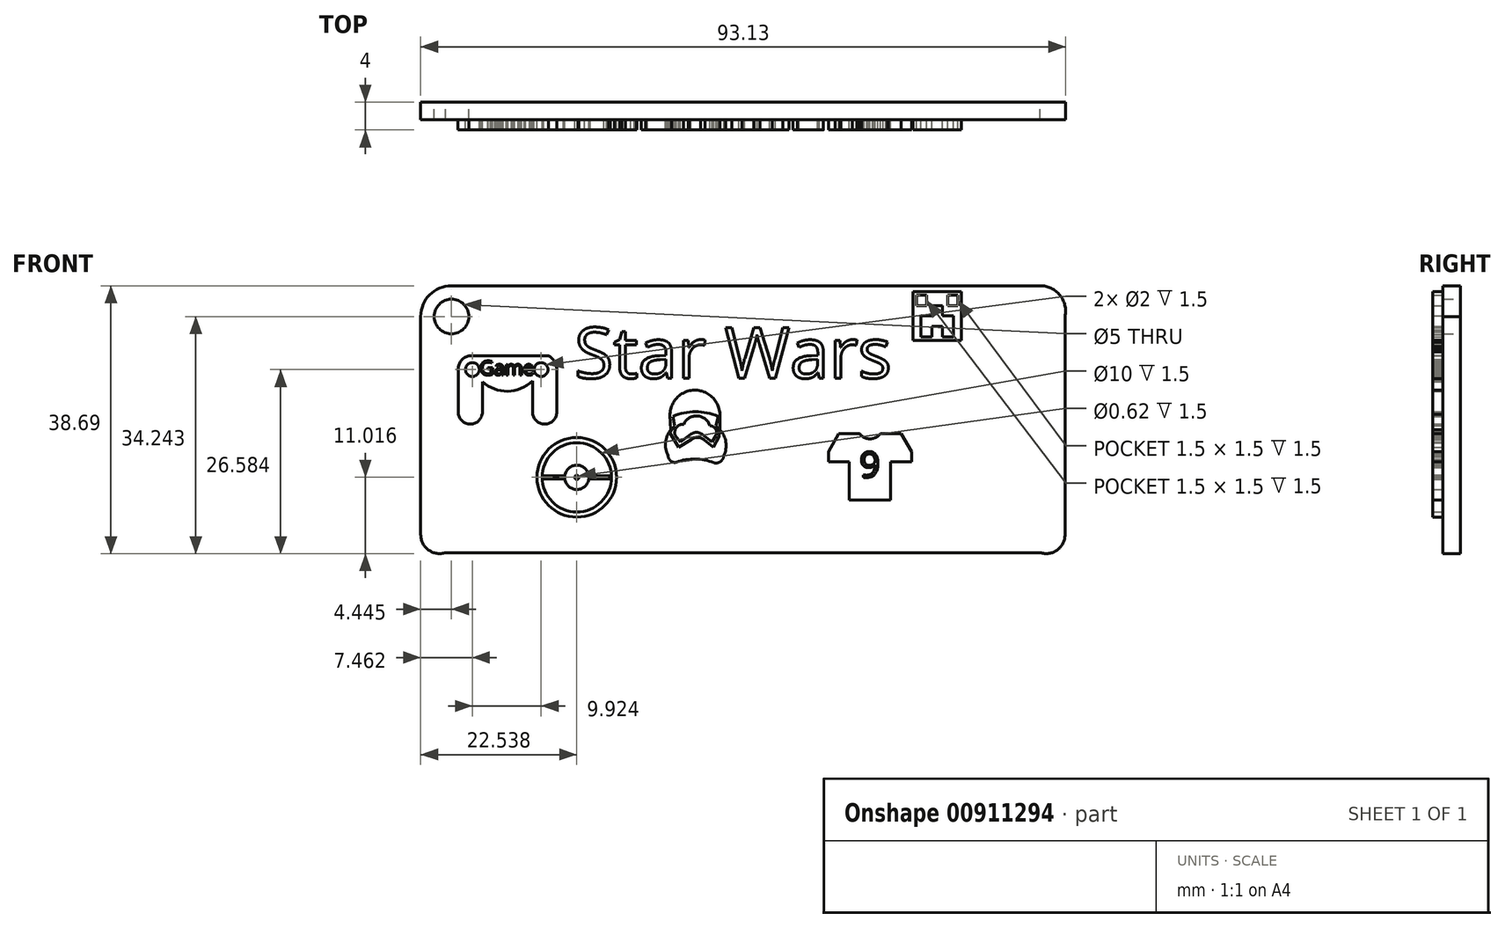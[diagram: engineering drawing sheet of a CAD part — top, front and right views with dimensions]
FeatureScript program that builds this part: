
annotation { "Feature Type Name" : "Feature", "Feature Type Description" : "" }
export const myFeature = defineFeature(function(context is Context, id is Id, definition is map)
    precondition{}
    {
        {
            var Q0;
            Q0=qCreatedBy(makeId("Front.planeOp"),FACE);
            var sketch = newSketch(context, id + "F0", { "sketchPlane" : qUnion([Q0])});
            skLineSegment(sketch, "E0", {"start": v(-44.85, 33.29) * mm, "end": v(40.15, 33.29) * mm});
            skLineSegment(sketch, "E1", {"start": v(-49.3, 28.84) * mm, "end": v(-49.3, -2.66) * mm});
            skLineSegment(sketch, "E2", {"start": v(-45.7, -5.26) * mm, "end": v(40.15, -5.26) * mm});
            skLineSegment(sketch, "E3", {"start": v(43.75, -2.66) * mm, "end": v(43.75, 28.84) * mm});
            skArc(sketch, "E4", {"start": v(-44.85, 33.29) * mm, "mid": v(-48, 31.99) * mm, "end": v(-49.3, 28.84) * mm});
            skArc(sketch, "E5", {"start": v(43.75, 28.84) * mm, "mid": v(43, 31.92) * mm, "end": v(40.15, 33.29) * mm});
            skArc(sketch, "E6", {"start": v(-49.3, -2.66) * mm, "mid": v(-48.16, -4.88) * mm, "end": v(-45.7, -5.26) * mm});
            skArc(sketch, "E7", {"start": v(40.15, -5.26) * mm, "mid": v(42.61, -4.88) * mm, "end": v(43.75, -2.66) * mm});
            skCircle(sketch, "E8", {"center": v(-44.85, 28.84) * mm, "radius": 2.5 * mm});
            skSolve(sketch);
        }
        {
            var Q0;
            Q0 = qSketchRegion(id + "F0", true);
            extrude(context, id + "F1", {"entities" : qUnion([Q0]), "depth" : 2.5 * mm, "offsetDistance" : 25 * mm});
        }
        {
            var Q0;
            Q0=makeQuery(id+"F1.opExtrude","CAP_FACE",FACE,{"disambiguationData":[OSD([sQuery(id+"F0.wireOp",EDGE,"E0"),sQuery(id+"F0.wireOp",EDGE,"E1"),sQuery(id+"F0.wireOp",EDGE,"E2"),sQuery(id+"F0.wireOp",EDGE,"E3"),sQuery(id+"F0.wireOp",EDGE,"E4"),sQuery(id+"F0.wireOp",EDGE,"E5"),sQuery(id+"F0.wireOp",EDGE,"E6"),sQuery(id+"F0.wireOp",EDGE,"E7"),sQuery(id+"F0.wireOp",EDGE,"E8")])],"isStart":false});
            var sketch = newSketch(context, id + "F2", { "sketchPlane" : qUnion([Q0])});
            skLineSegment(sketch, "E9", {"start": v(-42.35, 23.18) * mm, "end": v(-30.85, 23.18) * mm});
            skArc(sketch, "E10", {"start": v(-42.35, 23.18) * mm, "mid": v(-43.5, 22.4) * mm, "end": v(-43.9, 21.05) * mm});
            skArc(sketch, "E11", {"start": v(-30.85, 23.18) * mm, "mid": v(-29.94, 22.3) * mm, "end": v(-29.65, 21.05) * mm});
            skLineSegment(sketch, "E12", {"start": v(-43.9, 21.05) * mm, "end": v(-43.9, 15.05) * mm});
            skLineSegment(sketch, "E13", {"start": v(-29.65, 21.05) * mm, "end": v(-29.65, 15.05) * mm});
            skLineSegment(sketch, "E14", {"start": v(-40.4, 19.42) * mm, "end": v(-40.4, 15.05) * mm});
            skLineSegment(sketch, "E15", {"start": v(-33.15, 19.55) * mm, "end": v(-33.15, 15.05) * mm});
            skArc(sketch, "E16", {"start": v(-43.9, 15.05) * mm, "mid": v(-42.15, 13.3) * mm, "end": v(-40.4, 15.05) * mm});
            skArc(sketch, "E17", {"start": v(-33.15, 15.05) * mm, "mid": v(-31.4, 13.3) * mm, "end": v(-29.65, 15.05) * mm});
            skCircle(sketch, "E18", {"center": v(-31.91, 21.18) * mm, "radius": 1 * mm});
            skCircle(sketch, "E19", {"center": v(-41.84, 21.18) * mm, "radius": 1 * mm});
            skArc(sketch, "E20", {"start": v(-40.4, 19.42) * mm, "mid": v(-36.75, 18.05) * mm, "end": v(-33.15, 19.55) * mm});
            skText(sketch, "E21", { "text": "Game\n", "fontName": "OpenSans-Regular.ttf"});
            skLineSegment(sketch, "E22.bottom", {"start": v(21.78, 32.42) * mm, "end": v(28.78, 32.42) * mm});
            skLineSegment(sketch, "E22.top", {"start": v(21.78, 25.42) * mm, "end": v(28.78, 25.42) * mm});
            skLineSegment(sketch, "E22.left", {"start": v(21.78, 32.42) * mm, "end": v(21.78, 25.42) * mm});
            skLineSegment(sketch, "E22.right", {"start": v(28.78, 32.42) * mm, "end": v(28.78, 25.42) * mm});
            skLineSegment(sketch, "E23.bottom", {"start": v(22.28, 31.92) * mm, "end": v(23.78, 31.92) * mm});
            skLineSegment(sketch, "E23.top", {"start": v(22.28, 30.42) * mm, "end": v(23.78, 30.42) * mm});
            skLineSegment(sketch, "E23.left", {"start": v(22.28, 31.92) * mm, "end": v(22.28, 30.42) * mm});
            skLineSegment(sketch, "E23.right", {"start": v(23.78, 31.92) * mm, "end": v(23.78, 30.42) * mm});
            skLineSegment(sketch, "E24.bottom", {"start": v(26.78, 31.92) * mm, "end": v(28.28, 31.92) * mm});
            skLineSegment(sketch, "E24.top", {"start": v(26.78, 30.42) * mm, "end": v(28.28, 30.42) * mm});
            skLineSegment(sketch, "E24.left", {"start": v(26.78, 31.92) * mm, "end": v(26.78, 30.42) * mm});
            skLineSegment(sketch, "E24.right", {"start": v(28.28, 31.92) * mm, "end": v(28.28, 30.42) * mm});
            skLineSegment(sketch, "E25.bottom", {"start": v(24.53, 30.42) * mm, "end": v(26.03, 30.42) * mm});
            skLineSegment(sketch, "E25.left", {"start": v(24.53, 30.42) * mm, "end": v(24.53, 28.92) * mm});
            skLineSegment(sketch, "E25.right", {"start": v(26.03, 30.42) * mm, "end": v(26.03, 28.92) * mm});
            skLineSegment(sketch, "E26", {"start": v(24.53, 28.92) * mm, "end": v(22.93, 28.92) * mm});
            skLineSegment(sketch, "E27", {"start": v(22.93, 25.92) * mm, "end": v(22.93, 28.92) * mm});
            skLineSegment(sketch, "E28", {"start": v(27.63, 25.92) * mm, "end": v(27.63, 28.92) * mm});
            skLineSegment(sketch, "E29", {"start": v(27.63, 28.92) * mm, "end": v(26.03, 28.92) * mm});
            skLineSegment(sketch, "E30", {"start": v(24.53, 25.92) * mm, "end": v(22.93, 25.92) * mm});
            skLineSegment(sketch, "E31", {"start": v(27.63, 25.92) * mm, "end": v(26.03, 25.92) * mm});
            skPoint(sketch, "E32", {"position": v(22.93, 27.42) * mm});
            skLineSegment(sketch, "E33", {"start": v(24.53, 25.92) * mm, "end": v(24.53, 27.42) * mm});
            skLineSegment(sketch, "E34", {"start": v(26.03, 27.42) * mm, "end": v(24.53, 27.42) * mm});
            skLineSegment(sketch, "E35", {"start": v(26.03, 27.42) * mm, "end": v(26.03, 25.92) * mm});
            const initialGuessF2  = {"E21": [-0.0408, 0.0204, 1, 0, 0.00204]};
            skSetInitialGuess(sketch, initialGuessF2);
            skSolve(sketch);
        }
        {
            var Q0;
            Q0=makeQuery(id+"F2.imprint","IMPRINT",FACE,{"disambiguationData":[TD([[makeQuery(id+"F2.imprint","IMPRINT",EDGE,{"derivedFrom":sQuery(id+"F2.wireOp",EDGE,"E21.sketch_text.stroke-89")}),1.0]])]});
            var Q1;
            Q1=makeQuery(id+"F2.imprint","IMPRINT",FACE,{"disambiguationData":[TD([[makeQuery(id+"F2.imprint","IMPRINT",EDGE,{"derivedFrom":sQuery(id+"F2.wireOp",EDGE,"E21.sketch_text.stroke-39")}),1.0]])]});
            var Q2;
            Q2=makeQuery(id+"F2.imprint","IMPRINT",FACE,{"disambiguationData":[TD([[makeQuery(id+"F2.imprint","IMPRINT",EDGE,{"derivedFrom":sQuery(id+"F2.wireOp",EDGE,"E9")}),-1.0]])]});
            var Q3;
            Q3=makeQuery(id+"F2.imprint","IMPRINT",FACE,{"disambiguationData":[TD([[makeQuery(id+"F2.imprint","IMPRINT",EDGE,{"derivedFrom":sQuery(id+"F2.wireOp",EDGE,"E22.bottom")}),-1.0]])]});
            extrude(context, id + "F3", {"entities" : qUnion([Q0, Q1, Q2, Q3]), "operationType" : NewBodyOperationType.ADD, "depth" : 1.5 * mm, "offsetDistance" : 25 * mm});
        }
        {
            var Q0;
            {var subQ0=sQuery(id+"F0.wireOp",EDGE,"E1");var subQ1=sQuery(id+"F0.wireOp",EDGE,"E3");var subQ2=sQuery(id+"F0.wireOp",EDGE,"E0");var subQ3=sQuery(id+"F0.wireOp",EDGE,"E4");var subQ4=sQuery(id+"F0.wireOp",EDGE,"E5");var subQ5=sQuery(id+"F0.wireOp",EDGE,"E6");var subQ6=sQuery(id+"F0.wireOp",EDGE,"E7");var subQ7=sQuery(id+"F0.wireOp",EDGE,"E8");var subQ8=sQuery(id+"F0.wireOp",EDGE,"E2");Q0=makeQuery(id+"F3.boolean.opBoolean","SPLIT",FACE,{"disambiguationData":[TD([makeQuery(id+"F1.opExtrude","SWEPT_FACE",FACE,{"disambiguationData":[OSD([subQ2])]})])],"derivedFrom":makeQuery(id+"F1.opExtrude","CAP_FACE",FACE,{"disambiguationData":[OSD([subQ2,subQ0,subQ8,subQ1,subQ3,subQ4,subQ5,subQ6,subQ7])],"isStart":false})});}
            var sketch = newSketch(context, id + "F4", { "sketchPlane" : qUnion([Q0])});
            skLineSegment(sketch, "E36", {"start": v(11.07, 11.93) * mm, "end": v(14.07, 11.93) * mm});
            skLineSegment(sketch, "E37", {"start": v(17.07, 11.93) * mm, "end": v(20.07, 11.93) * mm});
            skLineSegment(sketch, "E38", {"start": v(20.07, 11.93) * mm, "end": v(21.57, 9.33) * mm});
            skLineSegment(sketch, "E39", {"start": v(21.57, 9.33) * mm, "end": v(21.57, 7.83) * mm});
            skPoint(sketch, "E40", {"position": v(18.57, 11.93) * mm});
            skPoint(sketch, "E41", {"position": v(12.57, 11.93) * mm});
            skLineSegment(sketch, "E42", {"start": v(21.57, 7.83) * mm, "end": v(18.57, 7.83) * mm});
            skLineSegment(sketch, "E43", {"start": v(18.57, 7.83) * mm, "end": v(18.57, 2.33) * mm});
            skLineSegment(sketch, "E44", {"start": v(18.57, 2.33) * mm, "end": v(12.57, 2.33) * mm});
            skLineSegment(sketch, "E45", {"start": v(12.57, 2.33) * mm, "end": v(12.57, 7.83) * mm});
            skLineSegment(sketch, "E46", {"start": v(12.57, 7.83) * mm, "end": v(9.57, 7.83) * mm});
            skLineSegment(sketch, "E47", {"start": v(9.57, 7.83) * mm, "end": v(9.57, 9.33) * mm});
            skLineSegment(sketch, "E48", {"start": v(9.57, 9.33) * mm, "end": v(11.07, 11.93) * mm});
            skArc(sketch, "E49", {"start": v(14.07, 11.93) * mm, "mid": v(15.57, 11.18) * mm, "end": v(17.07, 11.93) * mm});
            skText(sketch, "E50", { "text": "9\n", "fontName": "OpenSans-Regular.ttf"});
            skCircle(sketch, "E51", {"center": v(-26.76, 5.62) * mm, "radius": 5 * mm});
            skCircle(sketch, "E52", {"center": v(-26.76, 5.62) * mm, "radius": 1.75 * mm});
            skLineSegment(sketch, "E53.left", {"start": v(-25.03, 5.4) * mm, "end": v(-25.03, 5.85) * mm});
            skLineSegment(sketch, "E53.right", {"start": v(-21.77, 5.4) * mm, "end": v(-21.77, 5.85) * mm});
            skLineSegment(sketch, "E54.left", {"start": v(-28.5, 5.4) * mm, "end": v(-28.5, 5.85) * mm});
            skLineSegment(sketch, "E54.right", {"start": v(-31.76, 5.4) * mm, "end": v(-31.76, 5.85) * mm});
            skCircle(sketch, "E55", {"center": v(-26.76, 5.62) * mm, "radius": 5.75 * mm});
            skLineSegment(sketch, "E56.bottom", {"start": v(-21.96, 5.4) * mm, "end": v(-24.81, 5.4) * mm});
            skLineSegment(sketch, "E56.top", {"start": v(-21.96, 5.85) * mm, "end": v(-24.81, 5.85) * mm});
            skLineSegment(sketch, "E56.left", {"start": v(-21.96, 5.4) * mm, "end": v(-21.96, 5.85) * mm});
            skLineSegment(sketch, "E56.right", {"start": v(-24.81, 5.4) * mm, "end": v(-24.81, 5.85) * mm});
            skLineSegment(sketch, "E57.bottom", {"start": v(-28.71, 5.4) * mm, "end": v(-31.56, 5.4) * mm});
            skLineSegment(sketch, "E57.top", {"start": v(-28.71, 5.85) * mm, "end": v(-31.56, 5.85) * mm});
            skLineSegment(sketch, "E57.left", {"start": v(-28.71, 5.4) * mm, "end": v(-28.71, 5.85) * mm});
            skLineSegment(sketch, "E57.right", {"start": v(-31.56, 5.4) * mm, "end": v(-31.56, 5.85) * mm});
            skCircle(sketch, "E58", {"center": v(-26.76, 5.62) * mm, "radius": 0.3 * mm});
            const initialGuessF4  = {"E50": [0.01407, 0.00563, 1, 0, 0.0037]};
            skSetInitialGuess(sketch, initialGuessF4);
            skSolve(sketch);
        }
        {
            var Q0;
            Q0=makeQuery(id+"F4.imprint","IMPRINT",FACE,{"disambiguationData":[TD([[makeQuery(id+"F4.imprint","IMPRINT",EDGE,{"derivedFrom":sQuery(id+"F4.wireOp",EDGE,"E36")}),-1.0]])]});
            var Q1;
            Q1=makeQuery(id+"F4.imprint","IMPRINT",FACE,{"disambiguationData":[TD([[makeQuery(id+"F4.imprint","IMPRINT",EDGE,{"derivedFrom":sQuery(id+"F4.wireOp",EDGE,"E50.sketch_text.stroke-16")}),1.0]])]});
            var Q2;
            Q2=makeQuery(id+"F4.imprint","IMPRINT",FACE,{"disambiguationData":[TD([[makeQuery(id+"F4.imprint","IMPRINT",EDGE,{"derivedFrom":sQuery(id+"F4.wireOp",EDGE,"E55")}),1.0]])]});
            var Q3;
            {var subQ0=sQuery(id+"F4.wireOp",EDGE,"E54.left");var subQ1=sQuery(id+"F4.wireOp",EDGE,"E52");var subQ2=makeQuery(id+"F4.imprint","INTERSECT",VERTEX,{"derivedFrom":[subQ1,subQ0]});Q3=makeQuery(id+"F4.imprint","IMPRINT",FACE,{"disambiguationData":[TD([[makeQuery(id+"F4.imprint","IMPRINT",EDGE,{"disambiguationData":[TD([[subQ2,1.0]])],"derivedFrom":subQ1}),1.0]])]});}
            var Q4;
            {var subQ4=sQuery(id+"F4.wireOp",EDGE,"E54.bottom");Q4=makeQuery(id+"F4.imprint","IMPRINT",FACE,{"disambiguationData":[TD([[makeQuery(id+"F4.imprint","IMPRINT",EDGE,{"derivedFrom":subQ4}),-1.0]])]});}
            var Q5;
            {var subQ4=sQuery(id+"F4.wireOp",EDGE,"E53.bottom");Q5=makeQuery(id+"F4.imprint","IMPRINT",FACE,{"disambiguationData":[TD([[makeQuery(id+"F4.imprint","IMPRINT",EDGE,{"derivedFrom":subQ4}),1.0]])]});}
            var Q6;
            Q6=makeQuery(id+"F4.imprint","IMPRINT",FACE,{"disambiguationData":[TD([[makeQuery(id+"F4.imprint","IMPRINT",EDGE,{"derivedFrom":sQuery(id+"F4.wireOp",EDGE,"E57.bottom")}),-1.0]])]});
            var Q7;
            {var subQ0=sQuery(id+"F4.wireOp",EDGE,"E54.left");var subQ1=sQuery(id+"F4.wireOp",EDGE,"E52");var subQ2=makeQuery(id+"F4.imprint","INTERSECT",VERTEX,{"disambiguationData":[OD(1.0)],"derivedFrom":[subQ1,subQ0]});Q7=makeQuery(id+"F4.imprint","IMPRINT",FACE,{"disambiguationData":[TD([[makeQuery(id+"F4.imprint","IMPRINT",EDGE,{"disambiguationData":[TD([[subQ2,1.0]])],"derivedFrom":subQ1}),1.0]])]});}
            var Q8;
            Q8=makeQuery(id+"F4.imprint","IMPRINT",FACE,{"disambiguationData":[TD([[makeQuery(id+"F4.imprint","IMPRINT",EDGE,{"derivedFrom":sQuery(id+"F4.wireOp",EDGE,"E56.bottom")}),-1.0]])]});
            extrude(context, id + "F5", {"entities" : qUnion([Q0, Q1, Q2, Q3, Q4, Q5, Q6, Q7, Q8]), "operationType" : NewBodyOperationType.ADD, "depth" : 1.5 * mm, "offsetDistance" : 25 * mm});
        }
        {
            var Q0;
            {var subQ6=sQuery(id+"F0.wireOp",EDGE,"E1");var subQ9=sQuery(id+"F0.wireOp",EDGE,"E3");var subQ11=sQuery(id+"F0.wireOp",EDGE,"E0");var subQ12=makeQuery(id+"F1.opExtrude","SWEPT_FACE",FACE,{"disambiguationData":[OSD([subQ11])]});var subQ13=sQuery(id+"F0.wireOp",EDGE,"E4");var subQ16=sQuery(id+"F0.wireOp",EDGE,"E5");var subQ19=sQuery(id+"F0.wireOp",EDGE,"E6");var subQ22=sQuery(id+"F0.wireOp",EDGE,"E7");var subQ25=sQuery(id+"F0.wireOp",EDGE,"E8");var subQ28=sQuery(id+"F0.wireOp",EDGE,"E2");Q0=makeQuery(id+"F5.boolean.opBoolean","SPLIT",FACE,{"disambiguationData":[TD([subQ12])],"derivedFrom":makeQuery(id+"F3.boolean.opBoolean","SPLIT",FACE,{"disambiguationData":[TD([subQ12])],"derivedFrom":makeQuery(id+"F1.opExtrude","CAP_FACE",FACE,{"disambiguationData":[OSD([subQ11,subQ6,subQ28,subQ9,subQ13,subQ16,subQ19,subQ22,subQ25])],"isStart":false})})});}
            var sketch = newSketch(context, id + "F6", { "sketchPlane" : qUnion([Q0])});
            skText(sketch, "E59", { "text": "Star Wars\n", "fontName": "OpenSans-Regular.ttf"});
            skArc(sketch, "E60", {"start": v(-6.1, 14.7) * mm, "mid": v(-9.8, 18.21) * mm, "end": v(-13.3, 14.51) * mm});
            skArc(sketch, "E61", {"start": v(-6.96, 7.7) * mm, "mid": v(-9.67, 8.26) * mm, "end": v(-12.4, 7.79) * mm});
            skArc(sketch, "E62", {"start": v(-13.18, 12.52) * mm, "mid": v(-13.94, 10.68) * mm, "end": v(-13.56, 8.74) * mm});
            skLineSegment(sketch, "E63", {"start": v(-13.3, 14.51) * mm, "end": v(-13.18, 12.52) * mm});
            skArc(sketch, "E64", {"start": v(-13.56, 8.74) * mm, "mid": v(-13.2, 7.98) * mm, "end": v(-12.4, 7.79) * mm});
            skArc(sketch, "E65", {"start": v(-5.53, 8.73) * mm, "mid": v(-5.24, 10.7) * mm, "end": v(-6.1, 12.52) * mm});
            skArc(sketch, "E66", {"start": v(-6.96, 7.7) * mm, "mid": v(-6.01, 7.9) * mm, "end": v(-5.53, 8.73) * mm});
            skLineSegment(sketch, "E67", {"start": v(-12.65, 13.06) * mm, "end": v(-13.3, 12.03) * mm});
            skLineSegment(sketch, "E68", {"start": v(-13.3, 12.03) * mm, "end": v(-12.06, 9.97) * mm});
            skLineSegment(sketch, "E69", {"start": v(-6.1, 12.52) * mm, "end": v(-6.1, 14.7) * mm});
            skLineSegment(sketch, "E70", {"start": v(-6.22, 11.51) * mm, "end": v(-7.02, 9.97) * mm});
            skLineSegment(sketch, "E71", {"start": v(-12.06, 9.97) * mm, "end": v(-10.28, 11.04) * mm});
            skLineSegment(sketch, "E72", {"start": v(-7.02, 9.97) * mm, "end": v(-8.34, 11.04) * mm});
            skArc(sketch, "E73", {"start": v(-8.34, 11.04) * mm, "mid": v(-9.31, 11.38) * mm, "end": v(-10.28, 11.04) * mm});
            skArc(sketch, "E74", {"start": v(-7.53, 13.06) * mm, "mid": v(-9.35, 14.5) * mm, "end": v(-11.32, 13.28) * mm});
            skArc(sketch, "E75", {"start": v(-6.69, 11.66) * mm, "mid": v(-6.72, 12.6) * mm, "end": v(-7.53, 13.06) * mm});
            skArc(sketch, "E76", {"start": v(-11.32, 13.28) * mm, "mid": v(-12.37, 12.8) * mm, "end": v(-12.54, 11.66) * mm});
            skLineSegment(sketch, "E77", {"start": v(-11.8, 10.7) * mm, "end": v(-10.26, 11.85) * mm});
            skLineSegment(sketch, "E78", {"start": v(-7.2, 10.7) * mm, "end": v(-8.71, 11.85) * mm});
            skArc(sketch, "E79", {"start": v(-8.71, 11.85) * mm, "mid": v(-9.48, 12.1) * mm, "end": v(-10.26, 11.85) * mm});
            skLineSegment(sketch, "E80", {"start": v(-12.54, 11.66) * mm, "end": v(-11.8, 10.7) * mm});
            skLineSegment(sketch, "E81", {"start": v(-7.2, 10.7) * mm, "end": v(-6.69, 11.66) * mm});
            skLineSegment(sketch, "E82", {"start": v(-6.69, 13.06) * mm, "end": v(-6.14, 12.2) * mm});
            skLineSegment(sketch, "E83", {"start": v(-6.22, 11.51) * mm, "end": v(-6.14, 12.2) * mm});
            skLineSegment(sketch, "E84", {"start": v(-12.65, 13.06) * mm, "end": v(-12.9, 14.4) * mm});
            skLineSegment(sketch, "E85", {"start": v(-6.69, 13.06) * mm, "end": v(-6.36, 14.4) * mm});
            skArc(sketch, "E86", {"start": v(-6.36, 14.4) * mm, "mid": v(-9.63, 15.09) * mm, "end": v(-12.9, 14.4) * mm});
            const initialGuessF6  = {"E59": [-0.0271, 0.01995, 1, 0, 0.00734]};
            skSetInitialGuess(sketch, initialGuessF6);
            skSolve(sketch);
        }
        {
            var Q0;
            Q0=makeQuery(id+"F6.imprint","IMPRINT",FACE,{"disambiguationData":[TD([[makeQuery(id+"F6.imprint","IMPRINT",EDGE,{"derivedFrom":sQuery(id+"F6.wireOp",EDGE,"E59.sketch_text.stroke-0")}),-1.0]])]});
            var Q1;
            Q1=makeQuery(id+"F6.imprint","IMPRINT",FACE,{"disambiguationData":[TD([[makeQuery(id+"F6.imprint","IMPRINT",EDGE,{"derivedFrom":sQuery(id+"F6.wireOp",EDGE,"E59.sketch_text.stroke-25")}),-1.0]])]});
            var Q2;
            Q2=makeQuery(id+"F6.imprint","IMPRINT",FACE,{"disambiguationData":[TD([[makeQuery(id+"F6.imprint","IMPRINT",EDGE,{"derivedFrom":sQuery(id+"F6.wireOp",EDGE,"E59.sketch_text.stroke-71")}),-1.0]])]});
            var Q3;
            Q3=makeQuery(id+"F6.imprint","IMPRINT",FACE,{"disambiguationData":[TD([[makeQuery(id+"F6.imprint","IMPRINT",EDGE,{"derivedFrom":sQuery(id+"F6.wireOp",EDGE,"E59.sketch_text.stroke-84")}),-1.0]])]});
            var Q4;
            Q4=makeQuery(id+"F6.imprint","IMPRINT",FACE,{"disambiguationData":[TD([[makeQuery(id+"F6.imprint","IMPRINT",EDGE,{"derivedFrom":sQuery(id+"F6.wireOp",EDGE,"E59.sketch_text.stroke-131")}),-1.0]])]});
            var Q5;
            Q5=makeQuery(id+"F6.imprint","IMPRINT",FACE,{"disambiguationData":[TD([[makeQuery(id+"F6.imprint","IMPRINT",EDGE,{"derivedFrom":sQuery(id+"F6.wireOp",EDGE,"E59.sketch_text.stroke-144")}),-1.0]])]});
            var Q6;
            Q6=makeQuery(id+"F6.imprint","IMPRINT",FACE,{"disambiguationData":[TD([[makeQuery(id+"F6.imprint","IMPRINT",EDGE,{"derivedFrom":sQuery(id+"F6.wireOp",EDGE,"E59.sketch_text.stroke-44")}),-1.0]])]});
            var Q7;
            Q7=makeQuery(id+"F6.imprint","IMPRINT",FACE,{"disambiguationData":[TD([[makeQuery(id+"F6.imprint","IMPRINT",EDGE,{"derivedFrom":sQuery(id+"F6.wireOp",EDGE,"E59.sketch_text.stroke-104")}),-1.0]])]});
            var Q8;
            Q8=makeQuery(id+"F6.imprint","IMPRINT",FACE,{"disambiguationData":[TD([[makeQuery(id+"F6.imprint","IMPRINT",EDGE,{"derivedFrom":sQuery(id+"F6.wireOp",EDGE,"E60")}),1.0]])]});
            var Q9;
            Q9=makeQuery(id+"F6.imprint","IMPRINT",FACE,{"disambiguationData":[TD([[makeQuery(id+"F6.imprint","IMPRINT",EDGE,{"derivedFrom":sQuery(id+"F6.wireOp",EDGE,"E61")}),-1.0]])]});
            var Q10;
            Q10=makeQuery(id+"F6.imprint","IMPRINT",FACE,{"disambiguationData":[TD([[makeQuery(id+"F6.imprint","IMPRINT",EDGE,{"derivedFrom":sQuery(id+"F6.wireOp",EDGE,"EboQXFkx-ePQf-i1Pp-ILMp-x2kyPMlpTIYE")}),1.0]])]});
            var Q11;
            Q11=makeQuery(id+"F6.imprint","IMPRINT",FACE,{"disambiguationData":[TD([[makeQuery(id+"F6.imprint","IMPRINT",EDGE,{"derivedFrom":sQuery(id+"F6.wireOp",EDGE,"E74")}),1.0]])]});
            extrude(context, id + "F7", {"entities" : qUnion([Q0, Q1, Q2, Q3, Q4, Q5, Q6, Q7, Q8, Q9, Q10, Q11]), "operationType" : NewBodyOperationType.ADD, "depth" : 1.5 * mm, "offsetDistance" : 25 * mm});
        }
    });
